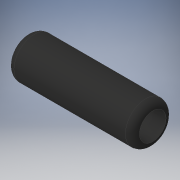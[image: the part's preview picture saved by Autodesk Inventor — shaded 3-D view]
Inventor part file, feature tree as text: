
AUTODESK INVENTOR PART (.ipt)
format: ipt  version: 2017 (Build 210142000, 142)  size: 125,952 bytes
history: native  units: in
note: dims shown in document units (in); Inventor stores cm internally (conversion verified against a paired STEP export)
features: fillet x2, revolve x1, sketch x1
ambient origin geometry x8: Origin, YZ Plane, XZ Plane, XY Plane, X Axis, Y Axis, Z Axis, Center Point
bodies: Body1 (feature_tree)
feature tree (4):
  revolve  "Revolution2"  [1 undecoded]
  fillet  "Fillet1"  Radius=4.313in
  fillet  "Fillet2"  Radius=0.4375in
  sketch  "Sketch3"  dims[d163=4.469in d164=0.25in d165=4.313in d166=0.4375in d167=0.0375in d168=90.0deg d169=0.25in d170=0.25in]
note: 1 required parameter value undecoded (feature->parameter linkage not recoverable at this tier; creation-order binding heuristic only, values carry confidence <= 0.55)
